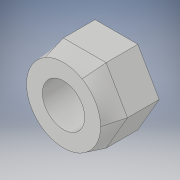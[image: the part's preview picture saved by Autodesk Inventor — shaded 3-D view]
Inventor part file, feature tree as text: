
AUTODESK INVENTOR PART (.ipt)
format: ipt  version: 2018 (Build 220112000, 112)  size: 145,408 bytes
history: native  units: in
note: dims shown in document units (in); Inventor stores cm internally (conversion verified against a paired STEP export)
features: sketch x4, extrude x2, plane x1, loft x1, projected_geometry x1
ambient origin geometry x8: Origin, YZ Plane, XZ Plane, XY Plane, X Axis, Y Axis, Z Axis, Center Point
bodies: Solid1 (feature_tree)
feature tree (9):
  extrude  "Extrusion1"  Depth=0.15in TaperAngle=0.0deg
  sketch  "Sketch2"  dims[d3=0.1in d4=0.35in]
  plane  "Work Plane1"
  loft  "Loft1"
  extrude  "Extrusion2"  TaperAngle=0.0deg  [1 undecoded]
  sketch  "Sketch1"  dims[d0=0.35in d1=0.15in d2=0.0in]
  projected_geometry  "Projected Loop1"
  sketch  "Sketch3"  dims[d5=0.0in d6=90.0deg d7=0.0in d8=90.0deg]
  sketch  "Sketch4"  dims[d9=0.2in d10=1.0in d11=0.0in]
note: 1 required parameter value undecoded (feature->parameter linkage not recoverable at this tier; creation-order binding heuristic only, values carry confidence <= 0.55)
